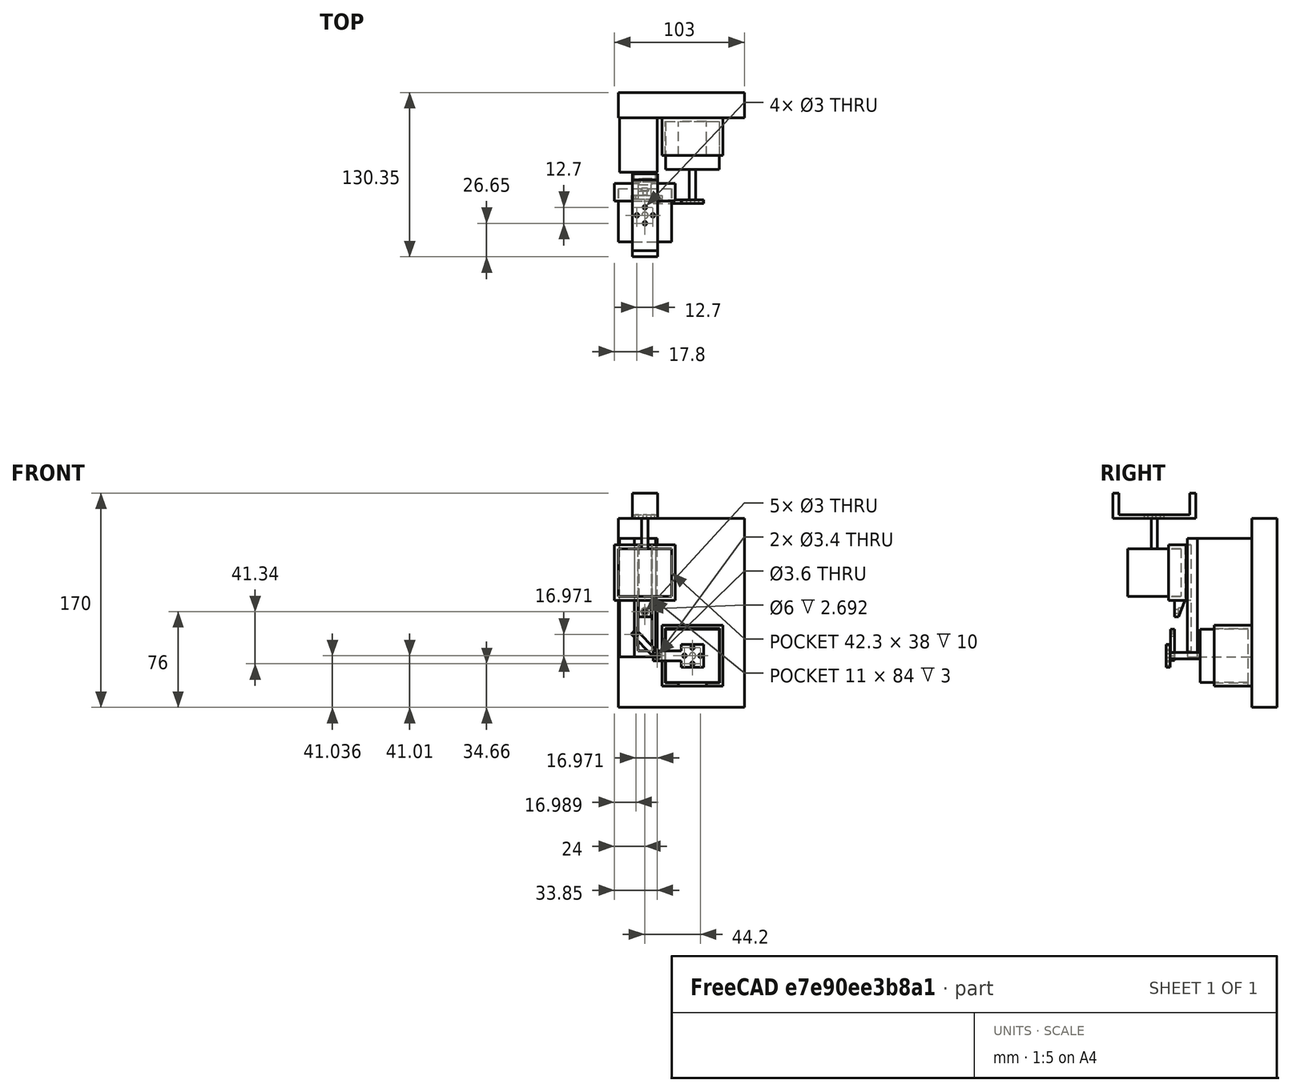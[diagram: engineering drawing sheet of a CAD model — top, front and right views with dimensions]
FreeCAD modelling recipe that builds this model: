
FCSTD DOCUMENT  (FreeCAD 0.18R16131 (Git))
Label: LayoutDesign
License: All rights reserved
LicenseURL: http://en.wikipedia.org/wiki/All_rights_reserved
objects: Part::Box×20, Part::Cut×19, Part::Cylinder×16, Part::MultiFuse×7, Part::Wedge×1
note: 63 computed .brp shape members not serialized (recipe doc carries the construction recipe); baked Part::Feature solids carry a one-line shape summary decoded from their .brp

FEATURE [Part::Box] Box  label="Motor"
  AttacherType = Attacher::AttachEngine3D
  Height = 38
  Length = 42.3
  Width = 42.3
FEATURE [Part::Cylinder] Cylinder  label="Rotor"
  Angle = 360
  AttacherType = Attacher::AttachEngine3D
  Height = 24
  Placement = pos=(21.15,21.15,38) rot=(0,0,1;0rad)
  Radius = 2.5
FEATURE [Part::MultiFuse] Fusion  label="17HS4401"
  Shapes = -> [Box,Cylinder]
FEATURE [Part::Cylinder] Cylinder004  label="H4"
  Angle = 360
  AttacherType = Attacher::AttachEngine3D
  Height = 10
  Placement = pos=(10,26.15,0) rot=(0,0,1;0rad)
  Radius = 1.5
FEATURE [Part::Box] Box002  label="Arm2"
  AttacherType = Attacher::AttachEngine3D
  Height = 20
  Length = 20
  Placement = pos=(0,60.5,0) rot=(0,0,1;0rad)
  Width = 5
FEATURE [Part::Cylinder] Cylinder001  label="H1"
  Angle = 360
  AttacherType = Attacher::AttachEngine3D
  Height = 10
  Placement = pos=(3.65,32.5,0) rot=(0,0,1;0rad)
  Radius = 1.5
FEATURE [Part::Cylinder] Cylinder002  label="H2"
  Angle = 360
  AttacherType = Attacher::AttachEngine3D
  Height = 10
  Placement = pos=(16.35,32.5,0) rot=(0,0,1;0rad)
  Radius = 1.5
FEATURE [Part::Box] Box001  label="Arm1"
  AttacherType = Attacher::AttachEngine3D
  Height = 20
  Length = 20
  Placement = pos=(0,-0.5,0) rot=(0,0,1;0rad)
  Width = 5
FEATURE [Part::Cylinder] Cylinder003  label="H3"
  Angle = 360
  AttacherType = Attacher::AttachEngine3D
  Height = 10
  Placement = pos=(10,38.85,0) rot=(0,0,1;0rad)
  Radius = 1.5
FEATURE [Part::Box] Box003  label="Base"
  AttacherType = Attacher::AttachEngine3D
  Height = 3
  Length = 20
  Width = 65
FEATURE [Part::Cut] Cut
  Base = -> Box003
  Tool = -> Cylinder001
FEATURE [Part::Cut] Cut001
  Base = -> Cut
  Tool = -> Cylinder004
FEATURE [Part::Cut] Cut002
  Base = -> Cut001
  Tool = -> Cylinder003
FEATURE [Part::Cut] Cut003
  Base = -> Cut002
  Tool = -> Cylinder002
FEATURE [Part::MultiFuse] Fusion001  label="Gripper"
  Placement = pos=(11.15,-11.35,62) rot=(0,0,1;0rad)
  Shapes = -> [Box001,Cut003,Box002]
FEATURE [Part::Cylinder] Cylinder005
  Angle = 360
  AttacherType = Attacher::AttachEngine3D
  Height = 10
  Placement = pos=(53,24,0) rot=(0,0,1;0rad)
  Radius = 1.5
FEATURE [Part::Cylinder] Cylinder006
  Angle = 360
  AttacherType = Attacher::AttachEngine3D
  Height = 10
  Placement = pos=(53,24,0) rot=(0,0,1;0rad)
  Radius = 1.5
FEATURE [Part::Box] Box004  label="Tray_Negative"
  AttacherType = Attacher::AttachEngine3D
  Height = 10
  Length = 38
  Placement = pos=(3,3,4) rot=(0,0,1;0rad)
  Width = 42.3
FEATURE [Part::Cylinder] Cylinder007
  Angle = 360
  AttacherType = Attacher::AttachEngine3D
  Height = 10
  Placement = pos=(53,24,-4) rot=(0,0,1;0rad)
  Radius = 3
FEATURE [Part::Box] Box005  label="Tray"
  AttacherType = Attacher::AttachEngine3D
  Height = 14
  Length = 44
  Width = 48.3
FEATURE [Part::Box] Box006  label="SlideSection"
  AttacherType = Attacher::AttachEngine3D
  Height = 5
  Length = 44
  Placement = pos=(0,19,-4) rot=(0,0,1;0rad)
  Width = 10.3
FEATURE [Part::Box] Box007  label="SliderConnect001"
  AttacherType = Attacher::AttachEngine3D
  Height = 3
  Length = 16
  Placement = pos=(41,19,6) rot=(0,0,1;0rad)
  Width = 10
FEATURE [Part::Cut] Cut004
  Base = -> Box005
  Tool = -> Box004
FEATURE [Part::Cut] Cut006  label="SlideConnector"
  Base = -> Box007
  Tool = -> Cylinder005
FEATURE [Part::Cut] Cut008  label="MainTray"
  Base = -> Cut004
  Tool = -> Box006
FEATURE [Part::Wedge] Wedge  label="SlideConnectorSupport"
  AttacherType = Attacher::AttachEngine3D
  Placement = pos=(44,19,6) rot=(-1,0,0;1.5708rad)
  X2max = 0
  X2min = 0
  Xmax = 13
  Xmin = 0
  Ymax = 5
  Ymin = 0
  Z2max = 10
  Z2min = 0
  Zmax = 10
  Zmin = 0
FEATURE [Part::MultiFuse] Fusion002
  Shapes = -> [Cut006,Wedge]
FEATURE [Part::MultiFuse] Fusion003  label="SliderTray"
  Shapes = -> [Fusion002,Cut008]
FEATURE [Part::Cut] Cut007
  Base = -> Fusion003
  Tool = -> Cylinder006
FEATURE [Part::Cut] Cut005  label="SildeFullTray"
  Base = -> Cut007
  Placement = pos=(-3,46.3,41) rot=(0.57735,0.57735,-0.57735;2.0944rad)
  Tool = -> Cylinder007
FEATURE [Part::Box] Box008  label="SlideModule"
  AttacherType = Attacher::AttachEngine3D
  Height = 8
  Length = 94
  Placement = pos=(-5,-3,0) rot=(0,0,1;0rad)
  Width = 17
FEATURE [Part::Box] Box009  label="SlideModuleNegative"
  AttacherType = Attacher::AttachEngine3D
  Height = 5
  Length = 84
  Placement = pos=(0,0,-2) rot=(0,0,1;0rad)
  Width = 11
FEATURE [Part::Cut] Cut009  label="SlidingModule"
  Base = -> Box008
  Placement = pos=(26.65,47.3,41) rot=(0.57735,-0.57735,-0.57735;4.18879rad)
  Tool = -> Box009
FEATURE [Part::Box] Box010  label="SlideSection001"
  AttacherType = Attacher::AttachEngine3D
  Height = 5
  Length = 44
  Placement = pos=(16.15,50.3,41) rot=(0.57735,0.57735,-0.57735;2.0944rad)
  Width = 10
FEATURE [Part::Cylinder] Cylinder008  label="Rotor001"
  Angle = 360
  AttacherType = Attacher::AttachEngine3D
  Height = 24
  Placement = pos=(21.15,21.15,38) rot=(0,0,1;0rad)
  Radius = 2.5
FEATURE [Part::Box] Box011  label="Motor001"
  AttacherType = Attacher::AttachEngine3D
  Height = 38
  Length = 42.3
  Width = 42.3
FEATURE [Part::MultiFuse] Fusion004  label="17HS4401-2"
  Placement = pos=(69,97,-48) rot=(1,0,0;1.5708rad)
  Shapes = -> [Box011,Cylinder008]
FEATURE [Part::Box] Box012  label="SlideMotorArm"
  AttacherType = Attacher::AttachEngine3D
  Height = 3
  Length = 18
  Placement = pos=(-4,21,0) rot=(0,0,1;0rad)
  Width = 18
FEATURE [Part::Box] Box013  label="SlideMotorArmExt"
  AttacherType = Attacher::AttachEngine3D
  Height = 3
  Length = 8
  Placement = pos=(1,-1,0) rot=(0,0,1;0rad)
  Width = 22
FEATURE [Part::Cylinder] Cylinder009
  Angle = 360
  AttacherType = Attacher::AttachEngine3D
  Height = 10
  Placement = pos=(-1.35,30,0) rot=(0,0,1;0rad)
  Radius = 1.5
FEATURE [Part::Cylinder] Cylinder010
  Angle = 360
  AttacherType = Attacher::AttachEngine3D
  Height = 10
  Placement = pos=(5,23.65,0) rot=(0,0,1;0rad)
  Radius = 1.5
FEATURE [Part::Cylinder] Cylinder011
  Angle = 360
  AttacherType = Attacher::AttachEngine3D
  Height = 10
  Placement = pos=(5,2,0) rot=(0,0,1;0rad)
  Radius = 1.8
FEATURE [Part::Cylinder] Cylinder012
  Angle = 360
  AttacherType = Attacher::AttachEngine3D
  Height = 10
  Placement = pos=(11.35,30,0) rot=(0,0,1;0rad)
  Radius = 1.5
FEATURE [Part::Cylinder] Cylinder013
  Angle = 360
  AttacherType = Attacher::AttachEngine3D
  Height = 10
  Placement = pos=(5,36.35,0) rot=(0,0,1;0rad)
  Radius = 1.5
FEATURE [Part::Cut] Cut010
  Base = -> Box012
  Tool = -> Cylinder013
FEATURE [Part::Cut] Cut012
  Base = -> Cut010
  Tool = -> Cylinder012
FEATURE [Part::Cut] Cut011
  Base = -> Cut012
  Tool = -> Cylinder009
FEATURE [Part::Cut] Cut013
  Base = -> Box013
  Tool = -> Cylinder011
FEATURE [Part::Cut] Cut014
  Base = -> Cut011
  Tool = -> Cylinder010
FEATURE [Part::MultiFuse] Fusion005  label="SlideMotorArmExtension"
  Placement = pos=(60.15,35,-21.85) rot=(0.57735,0.57735,-0.57735;2.0944rad)
  Shapes = -> [Cut014,Cut013]
FEATURE [Part::Box] Box014  label="SliderArm"
  AttacherType = Attacher::AttachEngine3D
  Height = 3
  Length = 30
  Width = 5
FEATURE [Part::Cylinder] Cylinder014
  Angle = 360
  AttacherType = Attacher::AttachEngine3D
  Height = 10
  Placement = pos=(3,2.5,0) rot=(0,0,1;0rad)
  Radius = 1.7
FEATURE [Part::Cylinder] Cylinder015
  Angle = 360
  AttacherType = Attacher::AttachEngine3D
  Height = 10
  Placement = pos=(27,2.5,0) rot=(0,0,1;0rad)
  Radius = 1.7
FEATURE [Part::Cut] Cut016
  Base = -> Box014
  Tool = -> Cylinder014
FEATURE [Part::Cut] Cut015  label="SlideArm"
  Base = -> Cut016
  Placement = pos=(41.4,38.5,-9.5) rot=(0.862856,0.357407,-0.357407;1.71777rad)
  Tool = -> Cylinder015
FEATURE [Part::MultiFuse] Fusion006  label="SlidingMotorConfig"
  Placement = pos=(-31.3,-1.5,-20.14) rot=(0,0,1;0rad)
  Shapes = -> [Fusion004,Fusion005,Cut015]
FEATURE [Part::Box] Box015  label="StaticTray"
  AttacherType = Attacher::AttachEngine3D
  Height = 48.3
  Length = 48.3
  Placement = pos=(91,0,0) rot=(0,0,1;0rad)
  Width = 30
FEATURE [Part::Box] Box016  label="StaticTrayNegative"
  AttacherType = Attacher::AttachEngine3D
  Height = 43.3
  Length = 43.3
  Placement = pos=(93.5,0,2.5) rot=(0,0,1;0rad)
  Width = 27
FEATURE [Part::Cut] Cut017  label="LinearMotorTray"
  Base = -> Box015
  Placement = pos=(-56.3,68.5,-71) rot=(0,0,1;0rad)
  Tool = -> Box016
FEATURE [Part::Box] Box017  label="MechBase"
  AttacherType = Attacher::AttachEngine3D
  Height = 150
  Length = 100
  Placement = pos=(0,98.5,-88) rot=(0,0,1;0rad)
  Width = 20
FEATURE [Part::Box] Box018  label="SliderBase"
  AttacherType = Attacher::AttachEngine3D
  Height = 94
  Length = 30
  Placement = pos=(1,55.3,-48) rot=(0,0,1;0rad)
  Width = 43.2
FEATURE [Part::Box] Box019  label="Cube"
  AttacherType = Attacher::AttachEngine3D
  Height = 10
  Length = 22
  Placement = pos=(47.85,68.5,-75) rot=(0,0,1;0rad)
  Width = 27
FEATURE [Part::Cut] Cut018  label="LinearTray"
  Base = -> Cut017
  Tool = -> Box019
